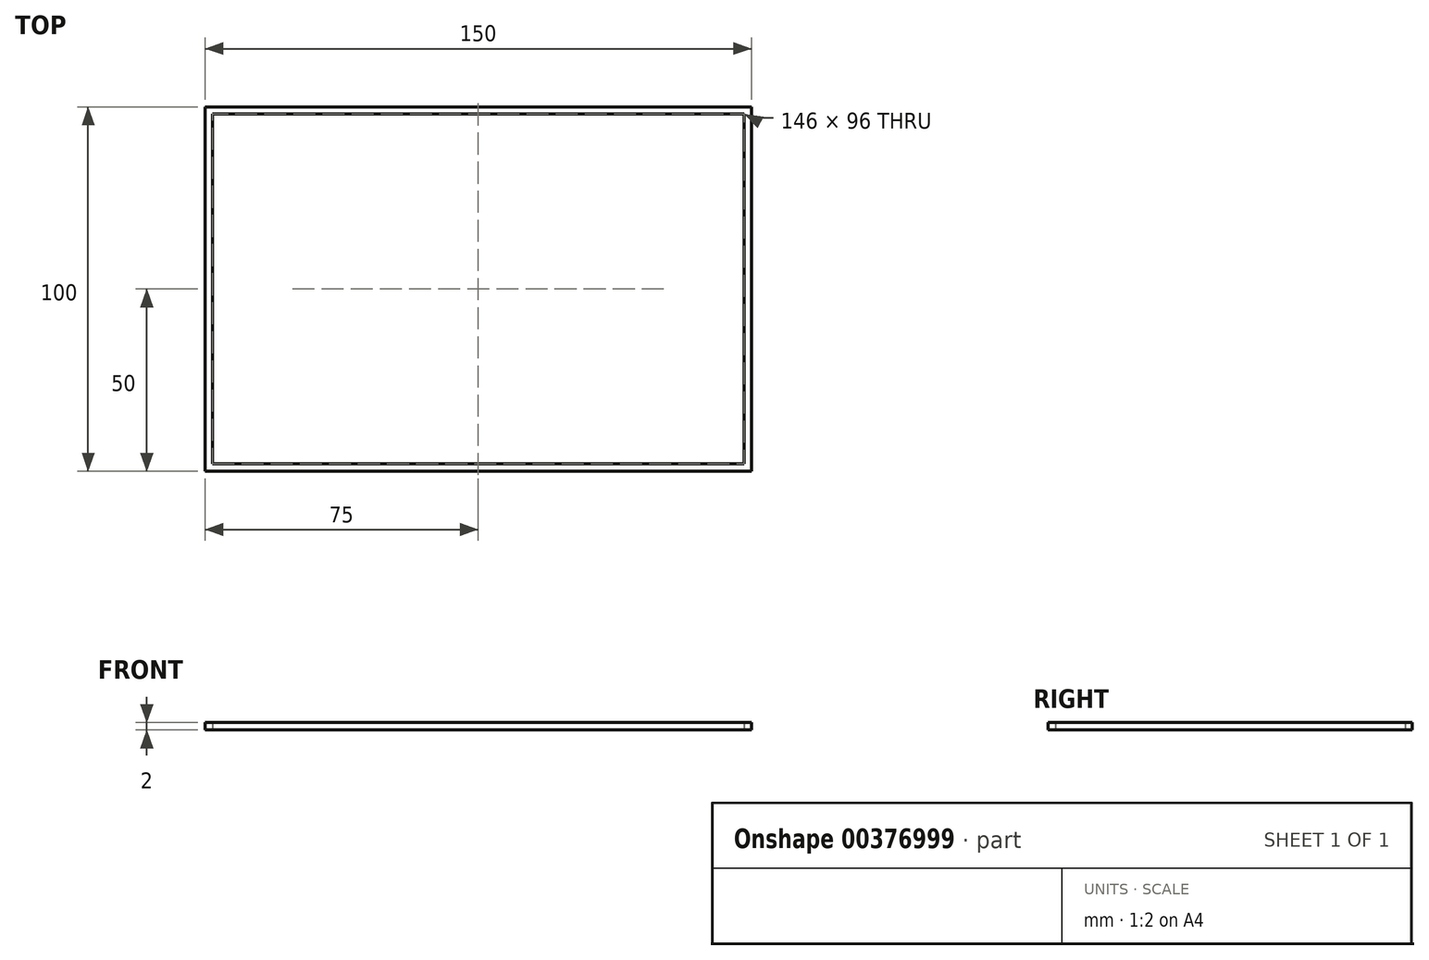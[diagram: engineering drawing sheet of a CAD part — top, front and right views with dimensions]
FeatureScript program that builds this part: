
annotation { "Feature Type Name" : "Feature", "Feature Type Description" : "" }
export const myFeature = defineFeature(function(context is Context, id is Id, definition is map)
    precondition{}
    {
        {
            assignVariable(context, id + "F0", {"name" : "width", "anyValue" : 2});
        }
        {
            var Q0;
            Q0=qCreatedBy(makeId("Top.planeOp"),FACE);
            var sketch = newSketch(context, id + "F1", { "sketchPlane" : qUnion([Q0])});
            skLineSegment(sketch, "E0.bottom", {"start": v(0, 0) * mm, "end": v(150, 0) * mm});
            skLineSegment(sketch, "E0.top", {"start": v(0, -100) * mm, "end": v(150, -100) * mm});
            skLineSegment(sketch, "E0.left", {"start": v(0, 0) * mm, "end": v(0, -100) * mm});
            skLineSegment(sketch, "E0.right", {"start": v(150, 0) * mm, "end": v(150, -100) * mm});
            skLineSegment(sketch, "E1.bottom", {"start": v(2, -2) * mm, "end": v(148, -2) * mm});
            skLineSegment(sketch, "E1.top", {"start": v(2, -98) * mm, "end": v(148, -98) * mm});
            skLineSegment(sketch, "E1.left", {"start": v(2, -2) * mm, "end": v(2, -98) * mm});
            skLineSegment(sketch, "E1.right", {"start": v(148, -2) * mm, "end": v(148, -98) * mm});
            skSolve(sketch);
        }
        {
            var Q0;
            Q0=makeQuery(id+"F1.imprint","IMPRINT",FACE,{"disambiguationData":[TD([[makeQuery(id+"F1.imprint","IMPRINT",EDGE,{"derivedFrom":sQuery(id+"F1.wireOp",EDGE,"E0.bottom")}),-1.0]])]});
            extrude(context, id + "F2", {"entities" : qUnion([Q0]), "depth" : (getVariable(context, 'width')) * mm});
        }
    });
